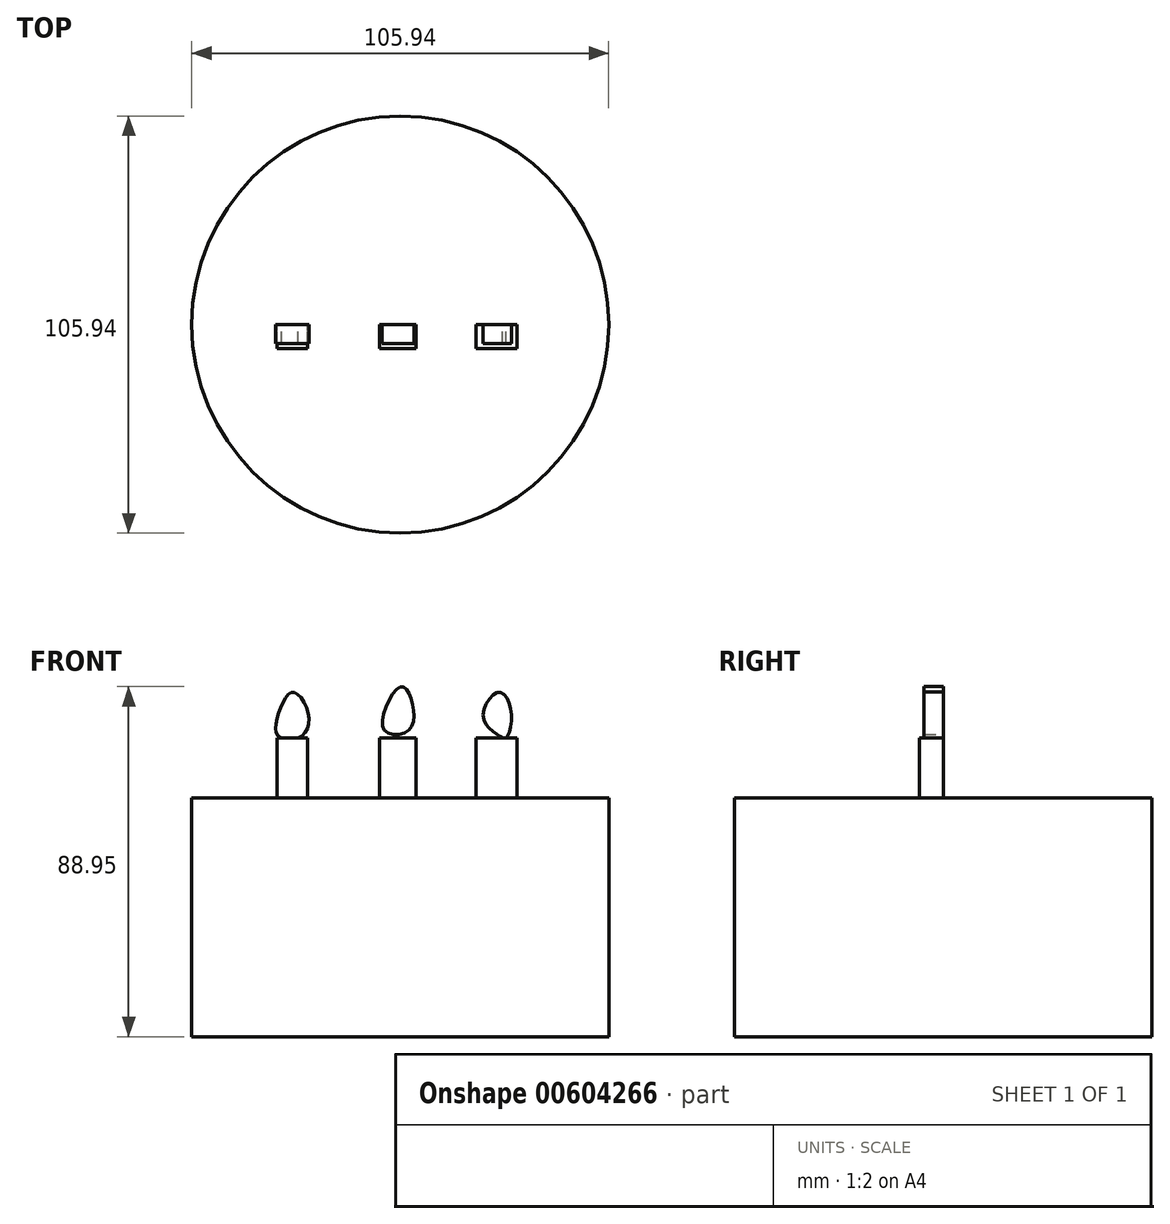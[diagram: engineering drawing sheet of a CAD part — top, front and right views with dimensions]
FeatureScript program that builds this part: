
annotation { "Feature Type Name" : "Feature", "Feature Type Description" : "" }
export const myFeature = defineFeature(function(context is Context, id is Id, definition is map)
    precondition{}
    {
        {
            var Q0;
            Q0=qCreatedBy(makeId("Top.planeOp"),FACE);
            var sketch = newSketch(context, id + "F0", { "sketchPlane" : qUnion([Q0])});
            skCircle(sketch, "E0", {"center": v(0, 0) * mm, "radius": 52.97 * mm});
            skSolve(sketch);
        }
        {
            var Q0;
            Q0 = qSketchRegion(id + "F0", true);
            extrude(context, id + "F1", {"entities" : qUnion([Q0]), "oppositeDirection" : true, "depth" : 60.7 * mm, "offsetDistance" : 25.4 * mm});
        }
        {
            var Q0;
            Q0=qCreatedBy(makeId("Front.planeOp"),FACE);
            var sketch = newSketch(context, id + "F2", { "sketchPlane" : qUnion([Q0])});
            skLineSegment(sketch, "E1.bottom", {"start": v(-31.26, 0) * mm, "end": v(-23.52, 0) * mm});
            skLineSegment(sketch, "E1.top", {"start": v(-31.26, 15.17) * mm, "end": v(-23.52, 15.17) * mm});
            skLineSegment(sketch, "E1.left", {"start": v(-31.26, 0) * mm, "end": v(-31.26, 15.17) * mm});
            skLineSegment(sketch, "E1.right", {"start": v(-23.52, 0) * mm, "end": v(-23.52, 15.17) * mm});
            skLineSegment(sketch, "E2.bottom", {"start": v(-5.26, 0) * mm, "end": v(4.02, 0) * mm});
            skLineSegment(sketch, "E2.top", {"start": v(-5.26, 15.17) * mm, "end": v(4.02, 15.17) * mm});
            skLineSegment(sketch, "E2.left", {"start": v(-5.26, 0) * mm, "end": v(-5.26, 15.17) * mm});
            skLineSegment(sketch, "E2.right", {"start": v(4.02, 0) * mm, "end": v(4.02, 15.17) * mm});
            skLineSegment(sketch, "E3.bottom", {"start": v(19.2, 0) * mm, "end": v(29.71, 0) * mm});
            skLineSegment(sketch, "E3.top", {"start": v(19.2, 15.17) * mm, "end": v(29.71, 15.17) * mm});
            skLineSegment(sketch, "E3.left", {"start": v(19.2, 0) * mm, "end": v(19.2, 15.17) * mm});
            skLineSegment(sketch, "E3.right", {"start": v(29.71, 0) * mm, "end": v(29.71, 15.17) * mm});
            skSolve(sketch);
        }
        {
            var Q0;
            Q0 = qSketchRegion(id + "F2", true);
            extrude(context, id + "F3", {"entities" : qUnion([Q0]), "operationType" : NewBodyOperationType.ADD, "depth" : 6.1 * mm, "offsetDistance" : 25.4 * mm});
        }
        {
            var Q0;
            Q0=qCreatedBy(makeId("Front.planeOp"),FACE);
            var sketch = newSketch(context, id + "F4", { "sketchPlane" : qUnion([Q0])});
            skFitSpline(sketch, "E4", {"points": [v(0, 28.18) * mm, v(-4.07, 21.78) * mm, v(-3.62, 16.74) * mm, v(1.64, 16.74) * mm, v(3.47, 20.86) * mm, v(2.1, 26.8) * mm, v(0, 28.18) * mm]});
            skFitSpline(sketch, "E5", {"points": [v(24.97, 26.8) * mm, v(21.08, 20.63) * mm, v(24.97, 15.83) * mm, v(26.8, 15.14) * mm, v(28.17, 21.78) * mm, v(24.97, 26.8) * mm]});
            skFitSpline(sketch, "E6", {"points": [v(-27.17, 26.8) * mm, v(-30.6, 22.23) * mm, v(-31.06, 15.83) * mm, v(-25.57, 15.37) * mm, v(-23.28, 21.09) * mm, v(-27.17, 26.8) * mm]});
            skSolve(sketch);
        }
        {
            var Q0;
            Q0 = qSketchRegion(id + "F4", true);
            extrude(context, id + "F5", {"entities" : qUnion([Q0]), "operationType" : NewBodyOperationType.ADD, "depth" : 4.83 * mm, "offsetDistance" : 25.4 * mm});
        }
    });
